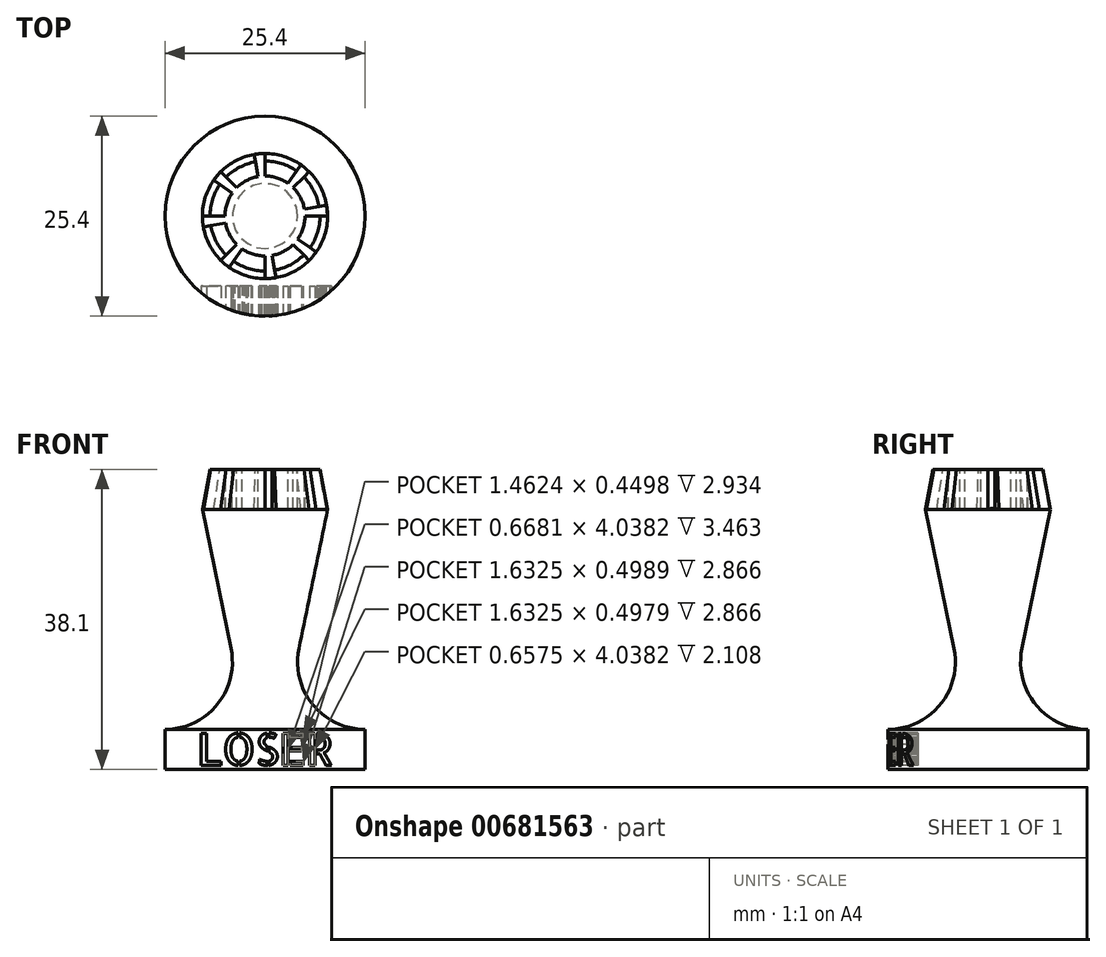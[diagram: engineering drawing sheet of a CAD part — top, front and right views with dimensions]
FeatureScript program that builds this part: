
annotation { "Feature Type Name" : "Feature", "Feature Type Description" : "" }
export const myFeature = defineFeature(function(context is Context, id is Id, definition is map)
    precondition{}
    {
        {
            var Q0;
            Q0=qCreatedBy(makeId("Front.planeOp"),FACE);
            var sketch = newSketch(context, id + "F0", { "sketchPlane" : qUnion([Q0])});
            skLineSegment(sketch, "E0", {"start": v(0, 0) * mm, "end": v(12.7, 0) * mm});
            skLineSegment(sketch, "E1", {"start": v(12.7, 0) * mm, "end": v(12.7, 5.08) * mm});
            skLineSegment(sketch, "E2", {"start": v(0, 38.1) * mm, "end": v(0, 0) * mm});
            skLineSegment(sketch, "E3", {"start": v(0, 33.02) * mm, "end": v(7.95, 33.02) * mm, "construction": true});
            skLineSegment(sketch, "E4", {"start": v(0, 38.1) * mm, "end": v(6.99, 38.1) * mm});
            skLineSegment(sketch, "E5", {"start": v(6.99, 38.1) * mm, "end": v(7.95, 33.02) * mm});
            skArc(sketch, "E6", {"start": v(4.32, 15.36) * mm, "mid": v(6.07, 8.23) * mm, "end": v(12.7, 5.08) * mm});
            skLineSegment(sketch, "E7", {"start": v(7.95, 33.02) * mm, "end": v(4.32, 15.36) * mm});
            skSolve(sketch);
        }
        {
            var Q0;
            Q0=makeQuery(id+"F0.imprint","IMPRINT",FACE,{"disambiguationData":[TD([[makeQuery(id+"F0.imprint","IMPRINT",EDGE,{"derivedFrom":sQuery(id+"F0.wireOp",EDGE,"E0")}),1.0]])]});
            var Q1;
            Q1=sQuery(id+"F0.wireOp",EDGE,"E2");
            revolve(context, id + "F1", {"entities" : qUnion([Q0]), "axis" : qUnion([Q1]), "revolveType" : RevolveType.FULL});
        }
        {
            var Q0;
            Q0=makeQuery(id+"F1.opRevolve","SWEPT_FACE",FACE,{"disambiguationData":[OSD([sQuery(id+"F0.wireOp",EDGE,"E4")])]});
            var sketch = newSketch(context, id + "F2", { "sketchPlane" : qUnion([Q0])});
            skCircle(sketch, "E8", {"center": v(0, 0) * mm, "radius": 5.08 * mm});
            skLineSegment(sketch, "E9", {"start": v(0, -5.08) * mm, "end": v(0, -7.95) * mm});
            skLineSegment(sketch, "E10", {"start": v(0.88, -5) * mm, "end": v(1.38, -7.83) * mm});
            skLineSegment(sketch, "E11.1.0", {"start": v(4.16, -2.91) * mm, "end": v(6.51, -4.56) * mm});
            skLineSegment(sketch, "E11.1.1", {"start": v(3.6, -3.6) * mm, "end": v(5.62, -5.62) * mm});
            skLineSegment(sketch, "E11.2.0", {"start": v(5, 0.88) * mm, "end": v(7.83, 1.38) * mm});
            skLineSegment(sketch, "E11.2.1", {"start": v(5.08, 0) * mm, "end": v(7.95, 0) * mm});
            skLineSegment(sketch, "E11.3.0", {"start": v(2.91, 4.16) * mm, "end": v(4.56, 6.51) * mm});
            skLineSegment(sketch, "E11.3.1", {"start": v(3.6, 3.6) * mm, "end": v(5.62, 5.62) * mm});
            skLineSegment(sketch, "E11.4.0", {"start": v(-0.88, 5) * mm, "end": v(-1.38, 7.83) * mm});
            skLineSegment(sketch, "E11.4.1", {"start": v(0, 5.08) * mm, "end": v(0, 7.95) * mm});
            skLineSegment(sketch, "E11.5.0", {"start": v(-4.16, 2.91) * mm, "end": v(-6.51, 4.56) * mm});
            skLineSegment(sketch, "E11.5.1", {"start": v(-3.6, 3.6) * mm, "end": v(-5.62, 5.62) * mm});
            skLineSegment(sketch, "E11.6.0", {"start": v(-5, -0.88) * mm, "end": v(-7.83, -1.38) * mm});
            skLineSegment(sketch, "E11.6.1", {"start": v(-5.08, 0) * mm, "end": v(-7.95, 0) * mm});
            skLineSegment(sketch, "E11.7.0", {"start": v(-2.91, -4.16) * mm, "end": v(-4.56, -6.51) * mm});
            skLineSegment(sketch, "E11.7.1", {"start": v(-3.6, -3.6) * mm, "end": v(-5.62, -5.62) * mm});
            skArc(sketch, "E12.trimOffspring", {"start": v(-7.95, 0) * mm, "mid": v(-7.92, -0.7) * mm, "end": v(-7.83, -1.38) * mm});
            skArc(sketch, "E13.trimOffspring", {"start": v(-5.62, -5.62) * mm, "mid": v(-5.11, -6.1) * mm, "end": v(-4.56, -6.51) * mm});
            skArc(sketch, "E14.trimOffspring", {"start": v(5.62, -5.62) * mm, "mid": v(6.1, -5.11) * mm, "end": v(6.51, -4.56) * mm});
            skArc(sketch, "E15.trimOffspring", {"start": v(5.62, 5.62) * mm, "mid": v(5.11, 6.1) * mm, "end": v(4.56, 6.51) * mm});
            skArc(sketch, "E16.trimOffspring", {"start": v(0, 7.95) * mm, "mid": v(-0.7, 7.92) * mm, "end": v(-1.38, 7.83) * mm});
            skArc(sketch, "E17.trimOffspring", {"start": v(0, -7.95) * mm, "mid": v(0.7, -7.92) * mm, "end": v(1.38, -7.83) * mm});
            skLineSegment(sketch, "E18", {"start": v(-6.51, 4.56) * mm, "end": v(-5.62, 5.62) * mm});
            skLineSegment(sketch, "E19", {"start": v(7.95, 0) * mm, "end": v(7.83, 1.38) * mm});
            skSolve(sketch);
        }
        {
            var Q0;
            Q0 = qSketchRegion(id + "F2", true);
            extrude(context, id + "F3", {"entities" : qUnion([Q0]), "operationType" : NewBodyOperationType.REMOVE, "oppositeDirection" : true, "depth" : 5.08 * mm, "offsetDistance" : 25.4 * mm});
        }
        {
            var Q0;
            Q0=qCreatedBy(makeId("Front.planeOp"),FACE);
            cPlane(context, id + "F4", {"entities" : qUnion([Q0]), "cplaneType" : CPlaneType.OFFSET, "offset" : 12.7 * mm, "width" : 152.4 * mm, "height" : 152.4 * mm});
        }
        {
            var Q0;
            Q0=qCreatedBy(id+"F4.planeOp",FACE);
            var sketch = newSketch(context, id + "F5", { "sketchPlane" : qUnion([Q0])});
            skText(sketch, "E20", { "text": "LOSER", "fontName": "AllertaStencil-Regular.ttf"});
            const initialGuessF5  = {"E20": [-0.00862, 0.00053, 1, 0, 0.00404]};
            skSetInitialGuess(sketch, initialGuessF5);
            skSolve(sketch);
        }
        {
            var Q0;
            Q0 = qSketchRegion(id + "F5", true);
            extrude(context, id + "F6", {"entities" : qUnion([Q0]), "operationType" : NewBodyOperationType.REMOVE, "oppositeDirection" : true, "depth" : 3.8 * mm, "offsetDistance" : 25.4 * mm});
        }
    });
